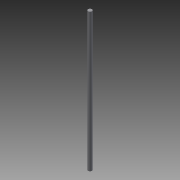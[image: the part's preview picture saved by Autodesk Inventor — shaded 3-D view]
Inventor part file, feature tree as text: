
AUTODESK INVENTOR PART (.ipt)
format: ipt  version: 2013 (Build 170138000, 138)  size: 60,928 bytes
history: native  units: in
note: dims shown in document units (in); Inventor stores cm internally (conversion verified against a paired STEP export)
features: extrude x1, sketch x1
ambient origin geometry x8: Origin, YZ Plane, XZ Plane, XY Plane, X Axis, Y Axis, Z Axis, Center Point
bodies: Solid1 (feature_tree)
feature tree (2):
  extrude  "Extrusion1"  Depth=18.25in TaperAngle=0.0deg
  sketch  "Sketch1"  dims[d0=0.5in d1=18.25in d2=0.0in]
